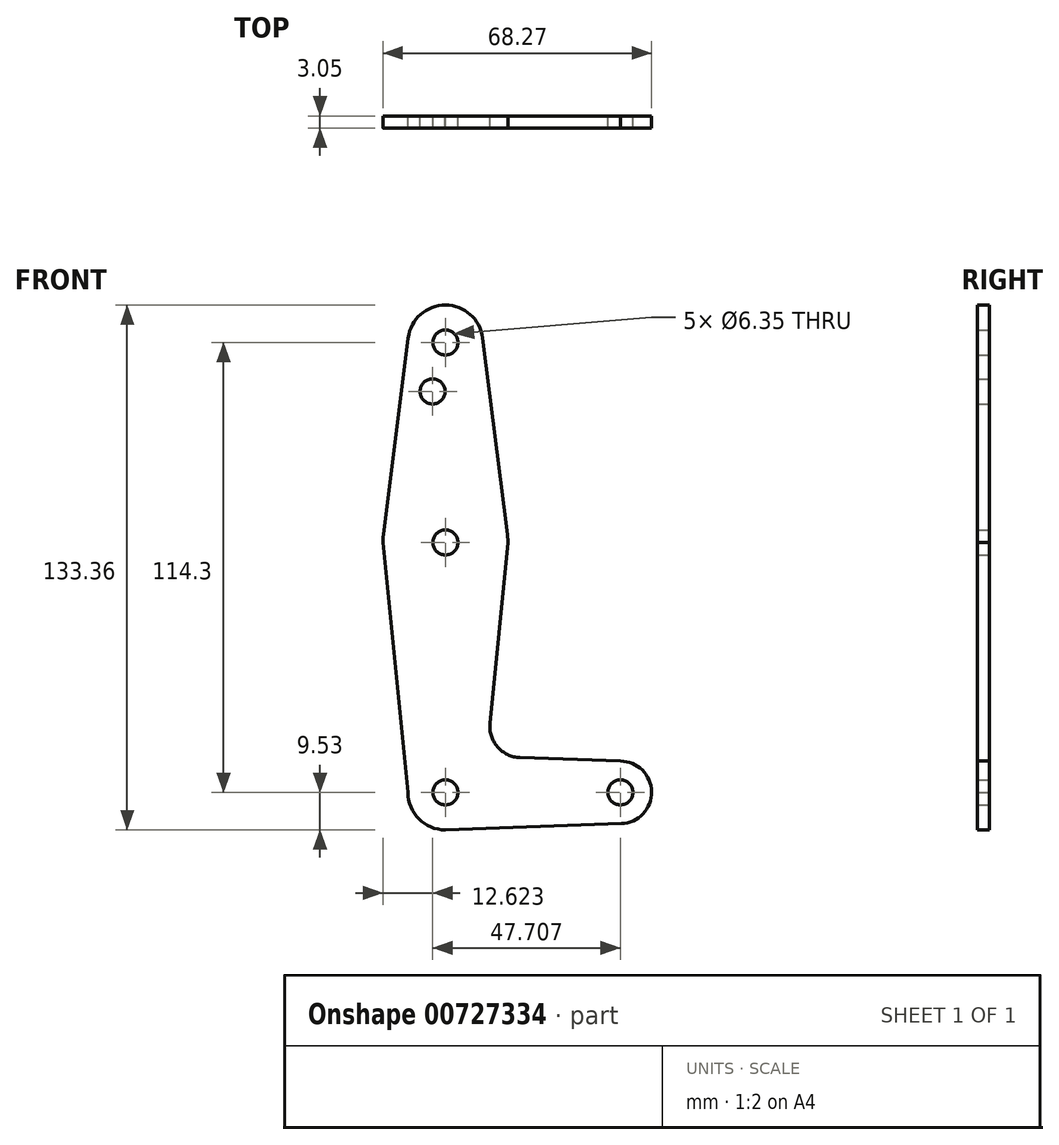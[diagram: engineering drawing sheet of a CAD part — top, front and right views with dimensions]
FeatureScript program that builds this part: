
annotation { "Feature Type Name" : "Feature", "Feature Type Description" : "" }
export const myFeature = defineFeature(function(context is Context, id is Id, definition is map)
    precondition{}
    {
        {
            var Q0;
            Q0=qCreatedBy(makeId("Front.planeOp"),FACE);
            var sketch = newSketch(context, id + "F0", { "sketchPlane" : qUnion([Q0])});
            skLineSegment(sketch, "E0", {"start": v(0, 0) * mm, "end": v(0, 114.3) * mm, "construction": true});
            skLineSegment(sketch, "E1", {"start": v(0, 0) * mm, "end": v(44.45, 0) * mm, "construction": true});
            skCircle(sketch, "E2", {"center": v(0, 0) * mm, "radius": 9.53 * mm});
            skCircle(sketch, "E3", {"center": v(44.45, 0) * mm, "radius": 7.94 * mm});
            skCircle(sketch, "E4", {"center": v(0, 114.3) * mm, "radius": 9.53 * mm});
            skLineSegment(sketch, "E5", {"start": v(0, -9.53) * mm, "end": v(44.73, -7.93) * mm});
            skLineSegment(sketch, "E6", {"start": v(44.45, 7.94) * mm, "end": v(18.94, 8.85) * mm});
            skCircle(sketch, "E7", {"center": v(0, 114.3) * mm, "radius": 3.18 * mm});
            skCircle(sketch, "E8", {"center": v(0, 63.5) * mm, "radius": 15.88 * mm});
            skLineSegment(sketch, "E9", {"start": v(9.45, 115.5) * mm, "end": v(15.75, 65.48) * mm});
            skLineSegment(sketch, "E10", {"start": v(-9.45, 115.5) * mm, "end": v(-15.75, 65.48) * mm});
            skLineSegment(sketch, "E11", {"start": v(-9.52, 0) * mm, "end": v(-15.88, 63.5) * mm});
            skLineSegment(sketch, "E12", {"start": v(15.88, 63.5) * mm, "end": v(11.32, 17.58) * mm});
            skCircle(sketch, "E13", {"center": v(-3.26, 101.88) * mm, "radius": 3.18 * mm});
            skCircle(sketch, "E14", {"center": v(0, 63.5) * mm, "radius": 3.18 * mm});
            skCircle(sketch, "E15", {"center": v(0, 0) * mm, "radius": 3.18 * mm});
            skCircle(sketch, "E16", {"center": v(44.45, 0) * mm, "radius": 3.18 * mm});
            skArc(sketch, "E17.filletArc", {"start": v(11.32, 17.58) * mm, "mid": v(13.24, 11.56) * mm, "end": v(18.94, 8.85) * mm});
            skSolve(sketch);
        }
        {
            var Q0;
            {var subQ1=sQuery(id+"F0.wireOp",EDGE,"E9");Q0=makeQuery(id+"F0.imprint","IMPRINT",FACE,{"disambiguationData":[TD([[makeQuery(id+"F0.imprint","IMPRINT",EDGE,{"derivedFrom":subQ1}),-1.0]])]});}
            var Q1;
            Q1=makeQuery(id+"F0.imprint","IMPRINT",FACE,{"disambiguationData":[TD([[makeQuery(id+"F0.imprint","IMPRINT",EDGE,{"derivedFrom":sQuery(id+"F0.wireOp",EDGE,"E7")}),-1.0]])]});
            var Q2;
            Q2=makeQuery(id+"F0.imprint","IMPRINT",FACE,{"disambiguationData":[TD([[makeQuery(id+"F0.imprint","IMPRINT",EDGE,{"derivedFrom":sQuery(id+"F0.wireOp",EDGE,"E14")}),-1.0]])]});
            var Q3;
            {var subQ0=sQuery(id+"F0.wireOp",EDGE,"E6");Q3=makeQuery(id+"F0.imprint","IMPRINT",FACE,{"disambiguationData":[TD([[makeQuery(id+"F0.imprint","IMPRINT",EDGE,{"derivedFrom":subQ0}),1.0]])]});}
            var Q4;
            Q4=makeQuery(id+"F0.imprint","IMPRINT",FACE,{"disambiguationData":[TD([[makeQuery(id+"F0.imprint","IMPRINT",EDGE,{"derivedFrom":sQuery(id+"F0.wireOp",EDGE,"E15")}),-1.0]])]});
            var Q5;
            Q5=makeQuery(id+"F0.imprint","IMPRINT",FACE,{"disambiguationData":[TD([[makeQuery(id+"F0.imprint","IMPRINT",EDGE,{"derivedFrom":sQuery(id+"F0.wireOp",EDGE,"E16")}),-1.0]])]});
            extrude(context, id + "F1", {"entities" : qUnion([Q0, Q1, Q2, Q3, Q4, Q5]), "depth" : 3.05 * mm, "offsetDistance" : 25.4 * mm});
        }
    });
